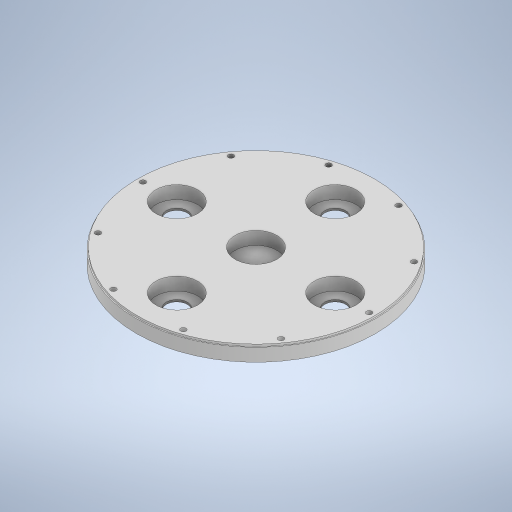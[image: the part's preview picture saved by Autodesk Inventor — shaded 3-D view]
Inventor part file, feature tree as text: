
AUTODESK INVENTOR PART (.ipt)
format: ipt  version: 2024.2 (Build 282272000, 272)  size: 424,960 bytes
history: native  units: in
note: dims shown in document units (in); Inventor stores cm internally (conversion verified against a paired STEP export)
features: extrude x6, sketch x6
ambient origin geometry x8: Origin, YZ Plane, XZ Plane, XY Plane, X Axis, Y Axis, Z Axis, Center Point
bodies: Solid1 (feature_tree)
feature tree (12):
  extrude  "Extrusion1"  Depth=0.5906in TaperAngle=360.0deg
  extrude  "Extrusion2"  Depth=0.0787in TaperAngle=360.0deg
  extrude  "Extrusion3"  Depth=1.1811in TaperAngle=0.0deg
  extrude  "Extrusion4"  Depth=0.5118in TaperAngle=0.0deg
  extrude  "Extrusion5"  Depth=3.937in TaperAngle=360.0deg
  extrude  "Extrusion6"  Depth=0.1409in
  sketch  "Sketch1"  dims[d1=3.937in d3=3.937in d19=360.0deg d21=360.0deg d22=0.5906in d23=0.0in d25=3.937in d27=3.937in d43=360.0deg d45=360.0deg]
  sketch  "Sketch2"  dims[d46=0.0787in d47=0.0in d49=3.937in d51=3.937in d52=360.0deg d53=360.0deg]
  sketch  "Sketch3"  dims[d55=3.937in d57=3.937in d58=360.0deg d59=360.0deg d60=1.1811in d61=0.0in]
  sketch  "Sketch4"  dims[d63=3.937in d65=3.937in d66=360.0deg d67=360.0deg d68=0.5118in d69=0.0in]
  sketch  "Sketch10"  dims[d71=3.937in d73=3.937in d74=360.0deg d75=360.0deg d76=3.937in d78=360.0deg]
  sketch  "Sketch14"  dims[d80=0.5118in d81=0.0in d82=0.4819in d85=3.937in d87=3.937in d88=360.0deg d89=360.0deg d90=0.1409in d91=0.0in d24=0.5in d48=0.5in d62=0.5in d70=0.5in]
